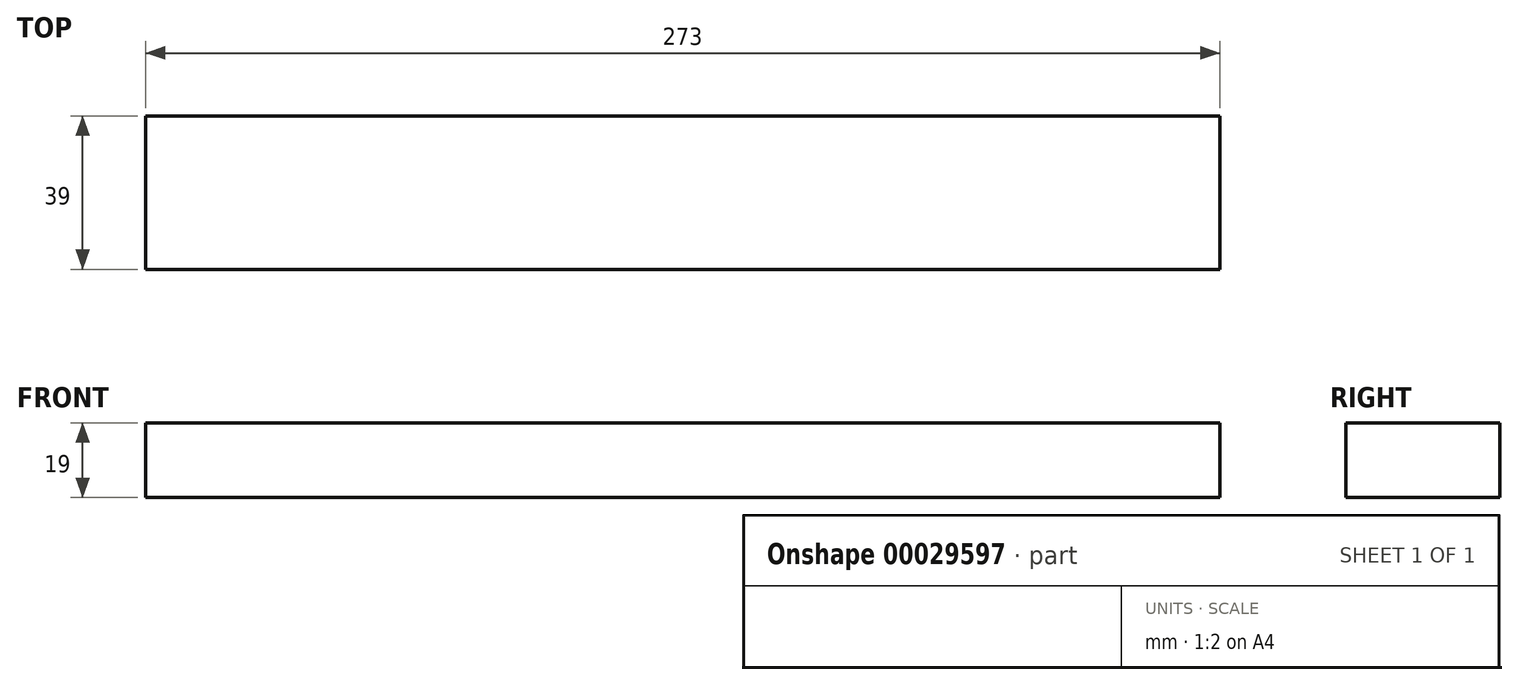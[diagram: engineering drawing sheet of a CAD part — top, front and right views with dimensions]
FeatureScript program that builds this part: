
annotation { "Feature Type Name" : "Feature", "Feature Type Description" : "" }
export const myFeature = defineFeature(function(context is Context, id is Id, definition is map)
    precondition{}
    {
        {
            var Q0;
            Q0=qCreatedBy(makeId("Top.planeOp"),FACE);
            var sketch = newSketch(context, id + "F0", { "sketchPlane" : qUnion([Q0])});
            skLineSegment(sketch, "E0.rect.bottom", {"start": v(136.5, -19.5) * mm, "end": v(-136.5, -19.5) * mm});
            skLineSegment(sketch, "E0.rect.top", {"start": v(136.5, 19.5) * mm, "end": v(-136.5, 19.5) * mm});
            skLineSegment(sketch, "E0.rect.left", {"start": v(136.5, -19.5) * mm, "end": v(136.5, 19.5) * mm});
            skLineSegment(sketch, "E0.rect.right", {"start": v(-136.5, -19.5) * mm, "end": v(-136.5, 19.5) * mm});
            skPoint(sketch, "E0.rect.middle", {"position": v(0, 0) * mm});
            skSolve(sketch);
        }
        {
            var Q0;
            Q0=makeQuery(id+"F0.imprint","IMPRINT",FACE,{"disambiguationData":[TD([[makeQuery(id+"F0.imprint","IMPRINT",EDGE,{"derivedFrom":sQuery(id+"F0.wireOp",EDGE,"E0.rect.bottom")}),-1.0]])]});
            extrude(context, id + "F1", {"entities" : qUnion([Q0]), "depth" : 19 * mm});
        }
    });
